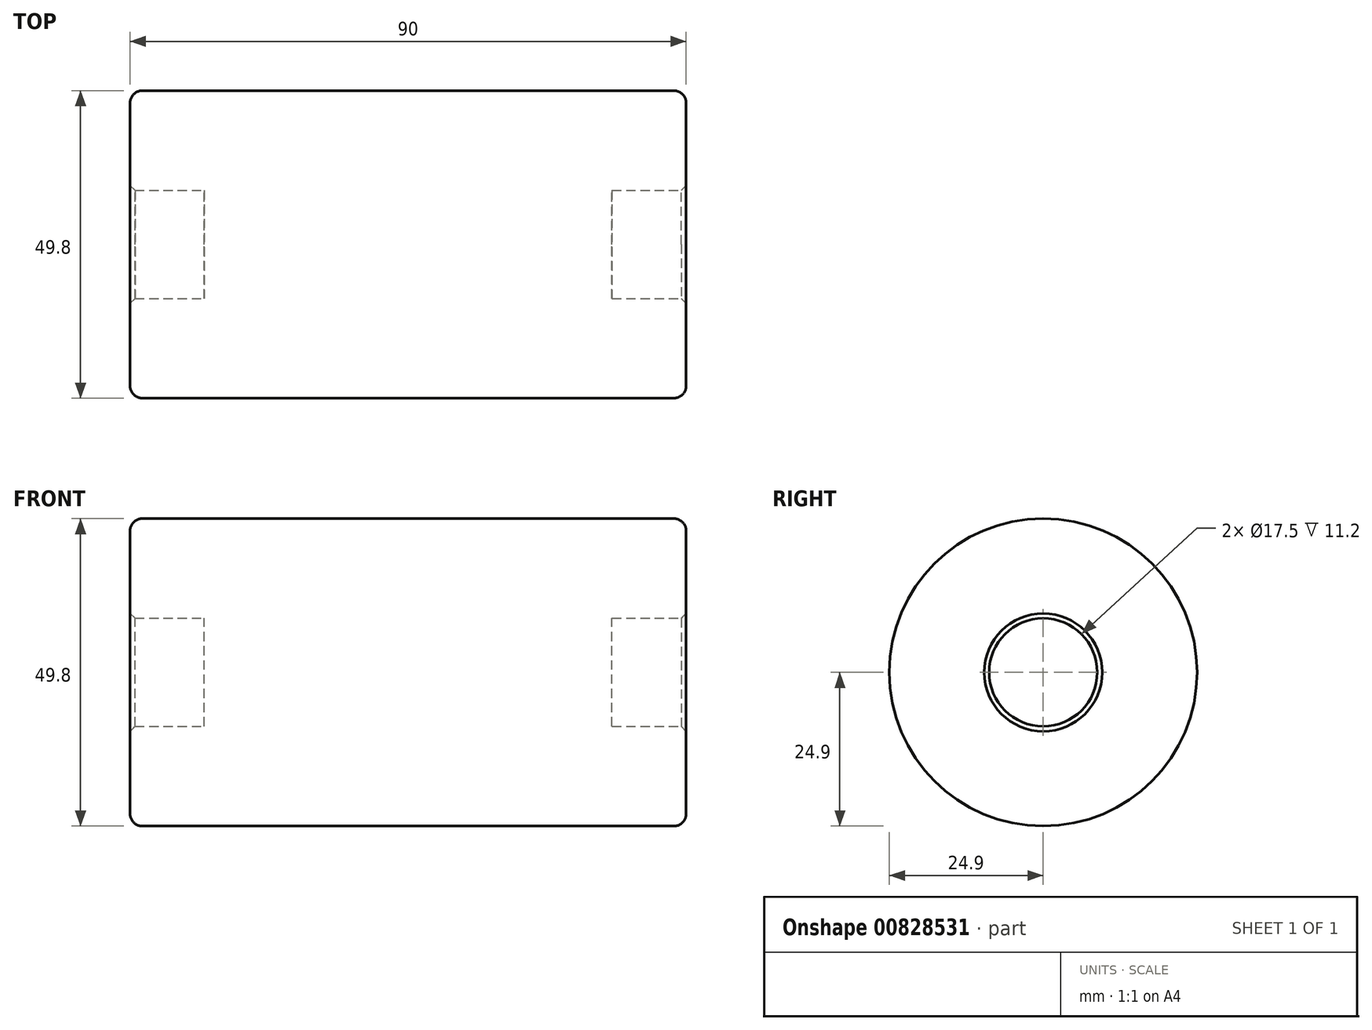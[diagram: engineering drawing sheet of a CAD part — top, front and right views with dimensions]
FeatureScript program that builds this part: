
annotation { "Feature Type Name" : "Feature", "Feature Type Description" : "" }
export const myFeature = defineFeature(function(context is Context, id is Id, definition is map)
    precondition{}
    {
        {
            var Q0;
            Q0=qCreatedBy(makeId("Top.planeOp"),FACE);
            var sketch = newSketch(context, id + "F0", { "sketchPlane" : qUnion([Q0])});
            skLineSegment(sketch, "E0", {"start": v(12, 0) * mm, "end": v(12, 8.75) * mm});
            skLineSegment(sketch, "E1", {"start": v(12, 8.75) * mm, "end": v(0, 8.75) * mm});
            skLineSegment(sketch, "E2", {"start": v(0, 8.75) * mm, "end": v(0, 24.9) * mm});
            skLineSegment(sketch, "E3", {"start": v(0, 24.9) * mm, "end": v(90, 24.9) * mm});
            skLineSegment(sketch, "E4", {"start": v(90, 24.9) * mm, "end": v(90, 8.75) * mm});
            skLineSegment(sketch, "E5", {"start": v(90, 8.75) * mm, "end": v(78, 8.75) * mm});
            skLineSegment(sketch, "E6", {"start": v(78, 8.75) * mm, "end": v(78, 0) * mm});
            skLineSegment(sketch, "E7", {"start": v(78, 0) * mm, "end": v(12, 0) * mm});
            skSolve(sketch);
        }
        {
            var Q0;
            Q0=makeQuery(id+"F0.imprint","IMPRINT",FACE,{"disambiguationData":[TD([[makeQuery(id+"F0.imprint","IMPRINT",EDGE,{"derivedFrom":sQuery(id+"F0.wireOp",EDGE,"E0")}),-1.0]])]});
            var Q1;
            Q1=sQuery(id+"F0.wireOp",EDGE,"E7");
            revolve(context, id + "F1", {"surfaceOperationType" : NewSurfaceOperationType.NEW, "entities" : qUnion([Q0]), "axis" : qUnion([Q1]), "revolveType" : RevolveType.FULL});
        }
        {
            var Q0;
            Q0=makeQuery(id+"F1.opRevolve","SWEPT_EDGE",EDGE,{"disambiguationData":[OSD([sQuery(id+"F0.wireOp",EDGE,"E2"),sQuery(id+"F0.wireOp",EDGE,"E3")])]});
            var Q1;
            Q1=makeQuery(id+"F1.opRevolve","SWEPT_EDGE",EDGE,{"disambiguationData":[OSD([sQuery(id+"F0.wireOp",EDGE,"E3"),sQuery(id+"F0.wireOp",EDGE,"E4")])]});
            fillet(context, id + "F2", {"entities" : qUnion([Q0, Q1]), "radius" : 2 * mm, "tangentPropagation" : true, "allowEdgeOverflow" : false});
        }
        {
            var Q0;
            Q0=makeQuery(id+"F1.opRevolve","SWEPT_EDGE",EDGE,{"disambiguationData":[OSD([sQuery(id+"F0.wireOp",EDGE,"E1"),sQuery(id+"F0.wireOp",EDGE,"E2")])]});
            var Q1;
            Q1=makeQuery(id+"F1.opRevolve","SWEPT_EDGE",EDGE,{"disambiguationData":[OSD([sQuery(id+"F0.wireOp",EDGE,"E4"),sQuery(id+"F0.wireOp",EDGE,"E5")])]});
            chamfer(context, id + "F3", {"entities" : qUnion([Q0, Q1]), "width" : 0.8 * mm, "tangentPropagation" : true});
        }
    });
